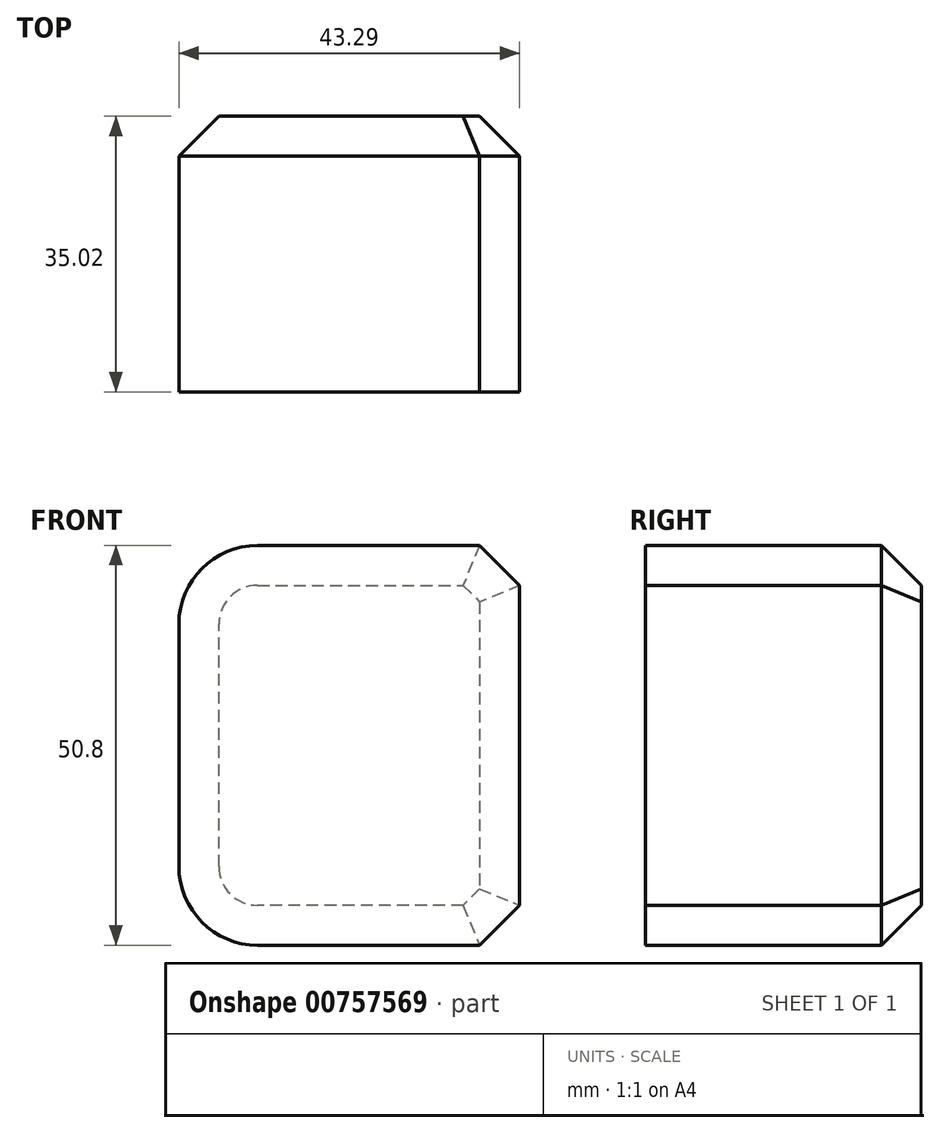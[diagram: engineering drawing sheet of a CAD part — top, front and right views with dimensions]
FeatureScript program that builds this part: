
annotation { "Feature Type Name" : "Feature", "Feature Type Description" : "" }
export const myFeature = defineFeature(function(context is Context, id is Id, definition is map)
    precondition{}
    {
        {
            var Q0;
            Q0=qCreatedBy(makeId("Top.planeOp"),FACE);
            var sketch = newSketch(context, id + "F0", { "sketchPlane" : qUnion([Q0])});
            skLineSegment(sketch, "E0.bottom", {"start": v(0, 0) * mm, "end": v(-43.3, 0) * mm});
            skLineSegment(sketch, "E0.top", {"start": v(0, 35.02) * mm, "end": v(-43.3, 35.02) * mm});
            skLineSegment(sketch, "E0.left", {"start": v(0, 0) * mm, "end": v(0, 35.02) * mm});
            skLineSegment(sketch, "E0.right", {"start": v(-43.3, 0) * mm, "end": v(-43.3, 35.02) * mm});
            skSolve(sketch);
        }
        {
            var Q0;
            Q0 = qSketchRegion(id + "F0", true);
            extrude(context, id + "F1", {"entities" : qUnion([Q0]), "depth" : 50.8 * mm, "offsetDistance" : 25.4 * mm});
        }
        {
            var Q0;
            Q0=makeQuery(id+"F1.opExtrude","CAP_EDGE",EDGE,{"disambiguationData":[OSD([sQuery(id+"F0.wireOp",EDGE,"E0.right")])],"isStart":false});
            fillet(context, id + "F2", {"entities" : qUnion([Q0]), "radius" : 10 * mm, "tangentPropagation" : true, "allowEdgeOverflow" : false});
        }
        {
            var Q0;
            Q0=makeQuery(id+"F1.opExtrude","CAP_EDGE",EDGE,{"disambiguationData":[OSD([sQuery(id+"F0.wireOp",EDGE,"E0.right")])],"isStart":true});
            fillet(context, id + "F3", {"entities" : qUnion([Q0]), "radius" : 10 * mm, "tangentPropagation" : true, "allowEdgeOverflow" : false});
        }
        {
            var Q0;
            Q0=makeQuery(id+"F1.opExtrude","CAP_EDGE",EDGE,{"disambiguationData":[OSD([sQuery(id+"F0.wireOp",EDGE,"E0.left")])],"isStart":true});
            chamfer(context, id + "F4", {"entities" : qUnion([Q0]), "width" : 5.08 * mm, "tangentPropagation" : true});
        }
        {
            var Q0;
            Q0=makeQuery(id+"F1.opExtrude","CAP_EDGE",EDGE,{"disambiguationData":[OSD([sQuery(id+"F0.wireOp",EDGE,"E0.left")])],"isStart":false});
            chamfer(context, id + "F5", {"entities" : qUnion([Q0]), "width" : 5.08 * mm, "tangentPropagation" : true});
        }
        {
            var Q0;
            Q0=makeQuery(id+"F4.opChamfer","BLEND_EDGE",EDGE,{"blendedFrom":[makeQuery(id+"F1.opExtrude","CAP_EDGE",EDGE,{"disambiguationData":[OSD([sQuery(id+"F0.wireOp",EDGE,"E0.left")])],"isStart":true}),makeQuery(id+"F1.opExtrude","SWEPT_FACE",FACE,{"disambiguationData":[OSD([sQuery(id+"F0.wireOp",EDGE,"E0.top")])]})],"blendedInto":[makeQuery(id+"F1.opExtrude","SWEPT_FACE",FACE,{"disambiguationData":[OSD([sQuery(id+"F0.wireOp",EDGE,"E0.top")])]})]});
            var Q1;
            Q1=makeQuery(id+"F1.opExtrude","CAP_EDGE",EDGE,{"disambiguationData":[OSD([sQuery(id+"F0.wireOp",EDGE,"E0.top")])],"isStart":false});
            var Q2;
            Q2=makeQuery(id+"F1.opExtrude","SWEPT_EDGE",EDGE,{"disambiguationData":[OSD([sQuery(id+"F0.wireOp",EDGE,"E0.top"),sQuery(id+"F0.wireOp",EDGE,"E0.left")])]});
            var Q3;
            Q3=makeQuery(id+"F2.opFillet","BLEND_EDGE",EDGE,{"blendedFrom":[makeQuery(id+"F1.opExtrude","CAP_EDGE",EDGE,{"disambiguationData":[OSD([sQuery(id+"F0.wireOp",EDGE,"E0.right")])],"isStart":false}),makeQuery(id+"F1.opExtrude","SWEPT_FACE",FACE,{"disambiguationData":[OSD([sQuery(id+"F0.wireOp",EDGE,"E0.top")])]})],"blendedInto":[makeQuery(id+"F1.opExtrude","SWEPT_FACE",FACE,{"disambiguationData":[OSD([sQuery(id+"F0.wireOp",EDGE,"E0.top")])]})]});
            var Q4;
            Q4=makeQuery(id+"F1.opExtrude","CAP_EDGE",EDGE,{"disambiguationData":[OSD([sQuery(id+"F0.wireOp",EDGE,"E0.top")])],"isStart":true});
            var Q5;
            Q5=makeQuery(id+"F5.opChamfer","BLEND_EDGE",EDGE,{"blendedFrom":[makeQuery(id+"F1.opExtrude","CAP_EDGE",EDGE,{"disambiguationData":[OSD([sQuery(id+"F0.wireOp",EDGE,"E0.left")])],"isStart":false}),makeQuery(id+"F1.opExtrude","SWEPT_FACE",FACE,{"disambiguationData":[OSD([sQuery(id+"F0.wireOp",EDGE,"E0.top")])]})],"blendedInto":[makeQuery(id+"F1.opExtrude","SWEPT_FACE",FACE,{"disambiguationData":[OSD([sQuery(id+"F0.wireOp",EDGE,"E0.top")])]})]});
            var Q6;
            Q6=makeQuery(id+"F3.opFillet","BLEND_EDGE",EDGE,{"blendedFrom":[makeQuery(id+"F1.opExtrude","CAP_EDGE",EDGE,{"disambiguationData":[OSD([sQuery(id+"F0.wireOp",EDGE,"E0.right")])],"isStart":true}),makeQuery(id+"F1.opExtrude","SWEPT_FACE",FACE,{"disambiguationData":[OSD([sQuery(id+"F0.wireOp",EDGE,"E0.top")])]})],"blendedInto":[makeQuery(id+"F1.opExtrude","SWEPT_FACE",FACE,{"disambiguationData":[OSD([sQuery(id+"F0.wireOp",EDGE,"E0.top")])]})]});
            var Q7;
            Q7=makeQuery(id+"F1.opExtrude","SWEPT_EDGE",EDGE,{"disambiguationData":[OSD([sQuery(id+"F0.wireOp",EDGE,"E0.top"),sQuery(id+"F0.wireOp",EDGE,"E0.right")])]});
            chamfer(context, id + "F6", {"entities" : qUnion([Q0, Q1, Q2, Q3, Q4, Q5, Q6, Q7]), "width" : 5.08 * mm, "tangentPropagation" : true});
        }
    });
